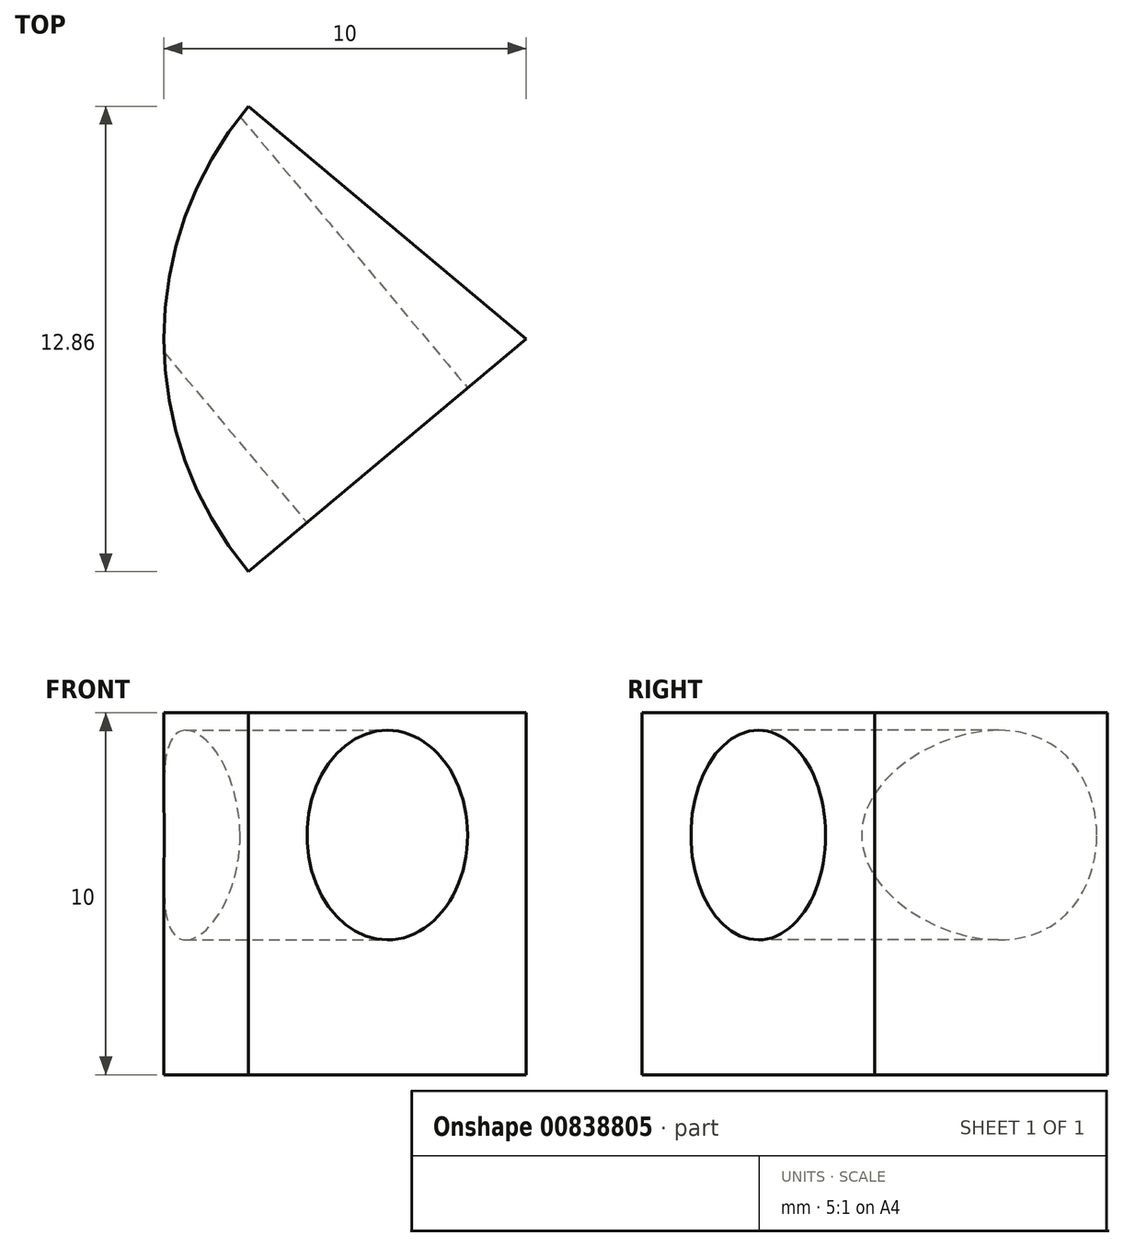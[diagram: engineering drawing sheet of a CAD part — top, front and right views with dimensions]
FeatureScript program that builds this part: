
annotation { "Feature Type Name" : "Feature", "Feature Type Description" : "" }
export const myFeature = defineFeature(function(context is Context, id is Id, definition is map)
    precondition{}
    {
        {
            var Q0;
            Q0=qCreatedBy(makeId("Front.planeOp"),FACE);
            var sketch = newSketch(context, id + "F0", { "sketchPlane" : qUnion([Q0])});
            skLineSegment(sketch, "E0.bottom", {"start": v(0, 3.38) * mm, "end": v(-10, 3.38) * mm});
            skLineSegment(sketch, "E0.top", {"start": v(0, -6.62) * mm, "end": v(-10, -6.62) * mm});
            skLineSegment(sketch, "E0.left", {"start": v(0, 3.38) * mm, "end": v(0, -6.62) * mm});
            skLineSegment(sketch, "E0.right", {"start": v(-10, 3.38) * mm, "end": v(-10, -6.62) * mm});
            skSolve(sketch);
        }
        {
            var Q0;
            Q0=makeQuery(id+"F0.imprint","IMPRINT",FACE,{"disambiguationData":[TD([[makeQuery(id+"F0.imprint","IMPRINT",EDGE,{"derivedFrom":sQuery(id+"F0.wireOp",EDGE,"E0.bottom")}),1.0]])]});
            var Q1;
            Q1=sQuery(id+"F0.wireOp",EDGE,"E0.left");
            revolve(context, id + "F1", {"surfaceOperationType" : NewSurfaceOperationType.NEW, "entities" : qUnion([Q0]), "axis" : qUnion([Q1]), "revolveType" : RevolveType.SYMMETRIC, "angle" : 80 * degree});
        }
        {
            var Q0;
            Q0=makeQuery(id+"F1.opRevolve","CAP_FACE",FACE,{"disambiguationData":[OSD([sQuery(id+"F0.wireOp",EDGE,"E0.bottom"),sQuery(id+"F0.wireOp",EDGE,"E0.top"),sQuery(id+"F0.wireOp",EDGE,"E0.left"),sQuery(id+"F0.wireOp",EDGE,"E0.right")])],"isStart":true});
            var sketch = newSketch(context, id + "F2", { "sketchPlane" : qUnion([Q0])});
            skPoint(sketch, "E1", {"position": v(-5, 0) * mm});
            skPoint(sketch, "E1.positionSnap0", {"position": v(-5, 3.38) * mm});
            skSolve(sketch);
        }
        {
            var Q0;
            Q0=sQuery(id+"F2.wireOp",VERTEX,"E1");
            var Q1;
            Q1=makeQuery(id+"F1.opRevolve","SWEPT_BODY",BODY,{"disambiguationData":[OSD([sQuery(id+"F0.wireOp",EDGE,"E0.bottom"),sQuery(id+"F0.wireOp",EDGE,"E0.top"),sQuery(id+"F0.wireOp",EDGE,"E0.left"),sQuery(id+"F0.wireOp",EDGE,"E0.right")])]});
            hole(context, id + "F3", {"style" : HoleStyle.C_BORE, "endStyle" : HoleEndStyle.THROUGH, "standardTappedOrClearance" : lookupTablePath({ "standard" : "ANSI", "size" : "#1 (0.23)", "type" : "Drilled" }), "standardBlindInLast" : lookupTablePath({ "standard" : "ANSI", "size" : "#1", "type" : "Drilled" }), "holeDiameter" : 5.8 * mm, "cBoreDiameter" : 5.8 * mm, "cBoreDepth" : 1.85 * mm, "majorDiameter" : 1.85 * mm, "isTappedThrough" : true, "tappedDepth" : 12 * mm, "tapClearance" : 3, "startFromSketch" : true, "locations" : qUnion([Q0]), "scope" : qUnion([Q1])});
        }
    });
